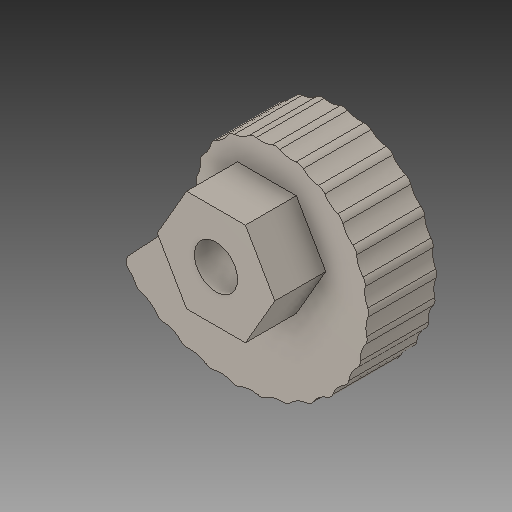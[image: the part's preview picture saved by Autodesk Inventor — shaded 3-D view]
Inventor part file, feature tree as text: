
AUTODESK INVENTOR PART (.ipt)
format: ipt  version: 2017 (Build 210142000, 142)  size: 184,832 bytes
history: native  units: in
note: dims shown in document units (in); Inventor stores cm internally (conversion verified against a paired STEP export)
features: fillet x1
ambient origin geometry x8: Origin, YZ Plane, XZ Plane, XY Plane, X Axis, Y Axis, Z Axis, Center Point
bodies: Solid1 (feature_tree)
feature tree (1):
  fillet  "Fillet1"  [1 undecoded]
note: 1 required parameter value undecoded (feature->parameter linkage not recoverable at this tier; creation-order binding heuristic only, values carry confidence <= 0.55)
